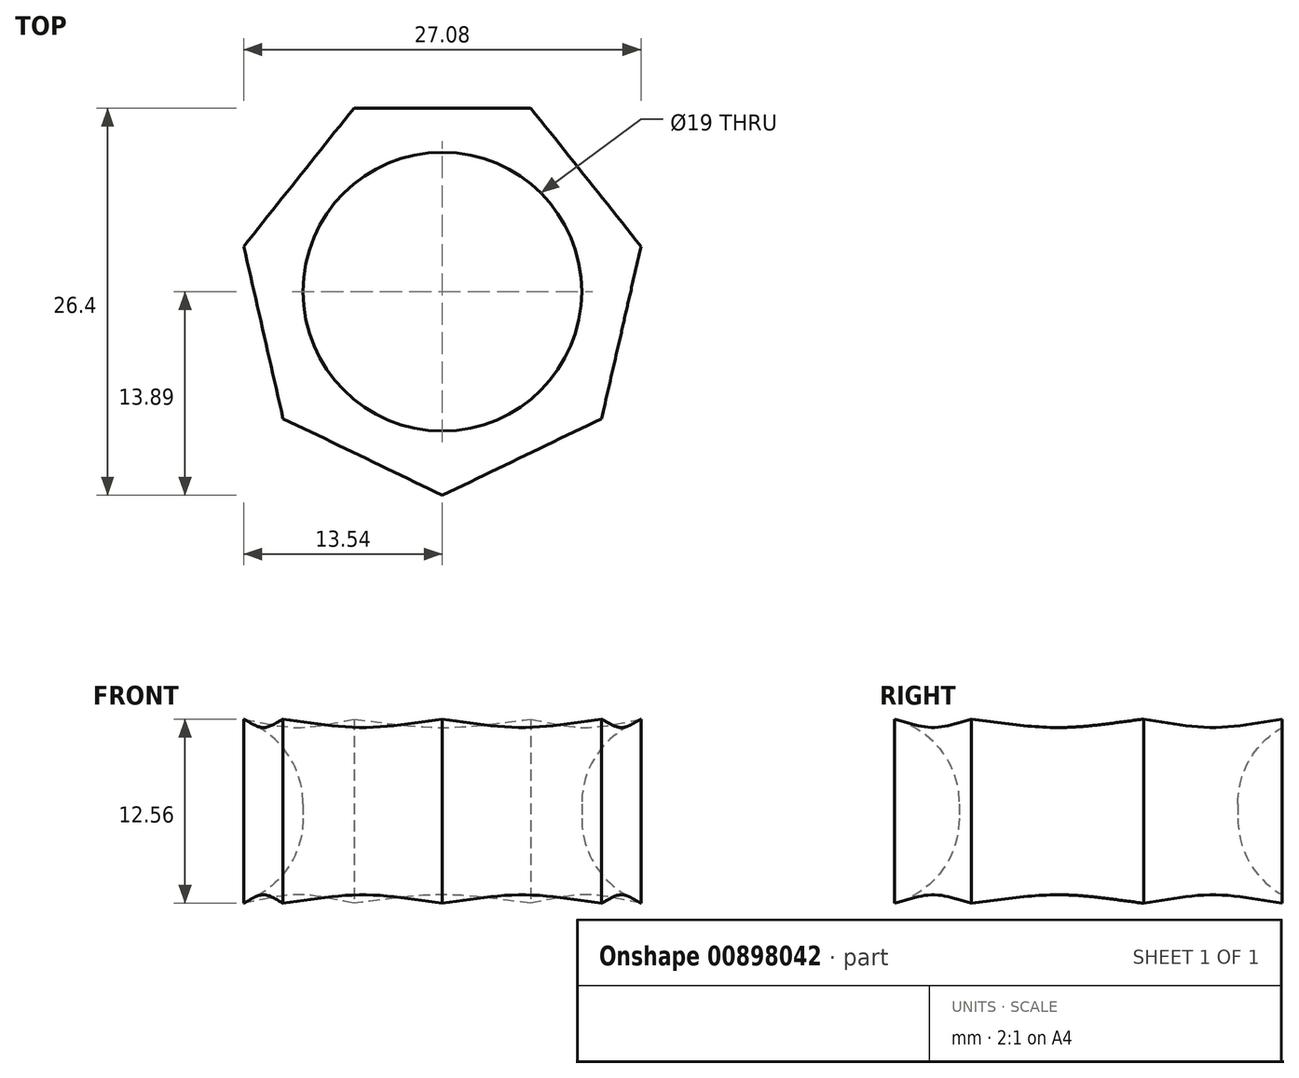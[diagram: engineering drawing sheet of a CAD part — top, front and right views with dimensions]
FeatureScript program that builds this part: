
annotation { "Feature Type Name" : "Feature", "Feature Type Description" : "" }
export const myFeature = defineFeature(function(context is Context, id is Id, definition is map)
    precondition{}
    {
        {
            var Q0;
            Q0=qCreatedBy(makeId("Top.planeOp"),FACE);
            var sketch = newSketch(context, id + "F0", { "sketchPlane" : qUnion([Q0])});
            skCircle(sketch, "E0.cCircle", {"center": v(0, 0) * mm, "radius": 12.51 * mm, "construction": true});
            skLineSegment(sketch, "E0.0", {"start": v(-6.02, 12.51) * mm, "end": v(6.02, 12.51) * mm});
            skLineSegment(sketch, "E0.1", {"start": v(6.02, 12.51) * mm, "end": v(13.54, 3.09) * mm});
            skLineSegment(sketch, "E0.2", {"start": v(13.54, 3.09) * mm, "end": v(10.86, -8.66) * mm});
            skLineSegment(sketch, "E0.3", {"start": v(10.86, -8.66) * mm, "end": v(0, -13.89) * mm});
            skLineSegment(sketch, "E0.4", {"start": v(0, -13.89) * mm, "end": v(-10.86, -8.66) * mm});
            skLineSegment(sketch, "E0.5", {"start": v(-10.86, -8.66) * mm, "end": v(-13.54, 3.09) * mm});
            skLineSegment(sketch, "E0.6", {"start": v(-13.54, 3.09) * mm, "end": v(-6.02, 12.51) * mm});
            skPoint(sketch, "E0.0.midPoint", {"position": v(0, 12.51) * mm});
            skCircle(sketch, "E1", {"center": v(0, 0) * mm, "radius": 9.5 * mm});
            skSolve(sketch);
        }
        {
            var Q0;
            Q0 = qSketchRegion(id + "F0", true);
            extrude(context, id + "F1", {"entities" : qUnion([Q0]), "depth" : 13 * mm, "offsetDistance" : 25.4 * mm});
        }
        {
            var Q0;
            Q0=makeQuery(id+"F1.opExtrude","SWEPT_FACE",FACE,{"disambiguationData":[OSD([sQuery(id+"F0.wireOp",EDGE,"E1")])]});
            var Q1;
            Q1=makeQuery(id+"F1.opExtrude","CAP_EDGE",EDGE,{"disambiguationData":[OSD([sQuery(id+"F0.wireOp",EDGE,"E1")])],"isStart":true});
            fillet(context, id + "F2", {"entities" : qUnion([Q0, Q1]), "radius" : 6 * mm, "tangentPropagation" : true, "allowEdgeOverflow" : false});
        }
    });
